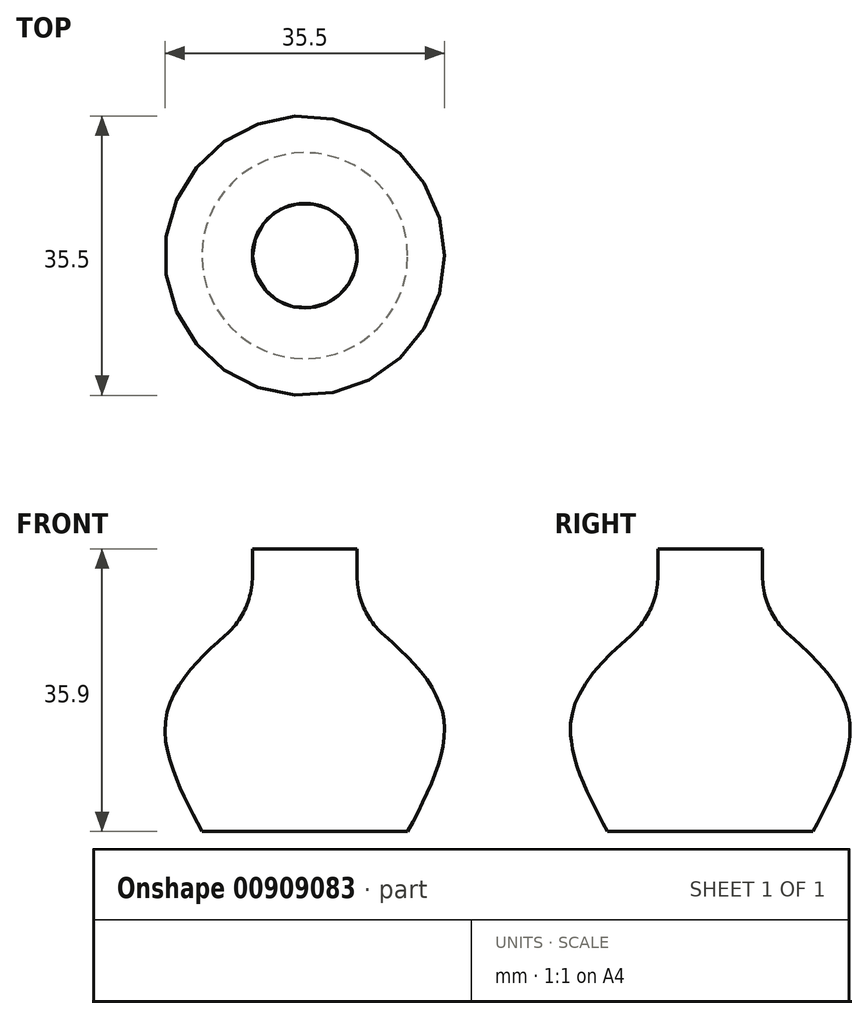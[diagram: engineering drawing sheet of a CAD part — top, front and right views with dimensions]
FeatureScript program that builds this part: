
annotation { "Feature Type Name" : "Feature", "Feature Type Description" : "" }
export const myFeature = defineFeature(function(context is Context, id is Id, definition is map)
    precondition{}
    {
        {
            var Q0;
            Q0=qCreatedBy(makeId("Top.planeOp"),FACE);
            var sketch = newSketch(context, id + "F0", { "sketchPlane" : qUnion([Q0])});
            skCircle(sketch, "E0", {"center": v(0, 0) * mm, "radius": 13.08 * mm});
            skSolve(sketch);
        }
        {
            var Q0;
            Q0=qCreatedBy(makeId("Top.planeOp"),FACE);
            cPlane(context, id + "F1", {"entities" : qUnion([Q0]), "cplaneType" : CPlaneType.OFFSET, "offset" : 14.4 * mm, "width" : 150 * mm, "height" : 150 * mm});
        }
        {
            var Q0;
            Q0=qCreatedBy(id+"F1.planeOp",FACE);
            var sketch = newSketch(context, id + "F2", { "sketchPlane" : qUnion([Q0])});
            skCircle(sketch, "E1", {"center": v(0, 0) * mm, "radius": 17.64 * mm});
            skSolve(sketch);
        }
        {
            var Q0;
            Q0=qCreatedBy(makeId("Top.planeOp"),FACE);
            cPlane(context, id + "F3", {"entities" : qUnion([Q0]), "cplaneType" : CPlaneType.OFFSET, "offset" : 27.8 * mm, "width" : 150 * mm, "height" : 150 * mm});
        }
        {
            var Q0;
            Q0=qCreatedBy(id+"F3.planeOp",FACE);
            var sketch = newSketch(context, id + "F4", { "sketchPlane" : qUnion([Q0])});
            skCircle(sketch, "E2", {"center": v(0, 0) * mm, "radius": 6.64 * mm});
            skSolve(sketch);
        }
        {
            var Q0;
            Q0=sQuery(id+"F0.wireOp",EDGE,"E0");
            var Q1;
            Q1=sQuery(id+"F2.wireOp",EDGE,"E1");
            var Q2;
            Q2=sQuery(id+"F4.wireOp",EDGE,"E2");
            loft(context, id + "F5", {"bodyType" : ToolBodyType.SURFACE, "wireProfilesArray" : [{ "wireProfileEntities" : qUnion([Q0]) }, { "wireProfileEntities" : qUnion([Q1]) }, { "wireProfileEntities" : qUnion([Q2]) }]});
        }
        {
            var Q0;
            Q0 = qConstructionFilter(qBodyType(qCreatedBy(id + "F4" ,EDGE), BodyType.WIRE), ConstructionObject.NO);
            extrude(context, id + "F6", {"bodyType" : ToolBodyType.SURFACE, "surfaceOperationType" : NewSurfaceOperationType.ADD, "surfaceEntities" : qUnion([Q0]), "depth" : 8.1 * mm, "offsetDistance" : 25 * mm});
        }
        {
            var Q0;
            {var subQ0=sQuery(id+"F4.wireOp",EDGE,"E2");Q0=makeQuery(id+"F6.join.opBoolean","MERGE",EDGE,{"derivedFrom":[makeQuery(id+"F5.opLoft","MID_CAP_EDGE",EDGE,{"disambiguationData":[OSD([subQ0])],"capPos":2.0}),makeQuery(id+"F6.opExtrude","CAP_EDGE",EDGE,{"disambiguationData":[OSD([subQ0])],"isStart":true})]});}
            fillet(context, id + "F7", {"entities" : qUnion([Q0]), "radius" : 10 * mm, "tangentPropagation" : true, "allowEdgeOverflow" : false});
        }
    });
